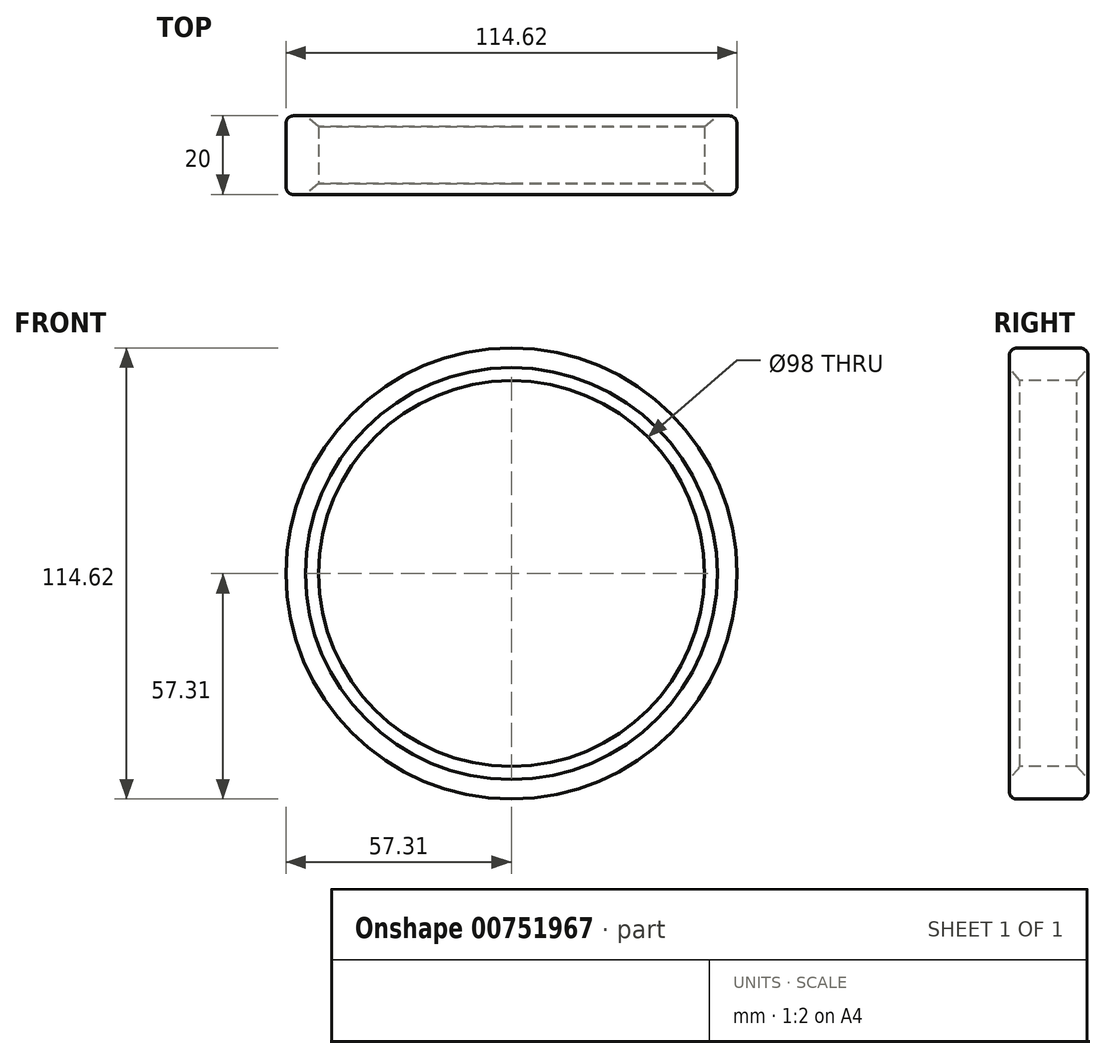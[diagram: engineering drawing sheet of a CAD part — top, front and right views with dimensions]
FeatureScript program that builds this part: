
annotation { "Feature Type Name" : "Feature", "Feature Type Description" : "" }
export const myFeature = defineFeature(function(context is Context, id is Id, definition is map)
    precondition{}
    {
        {
            var Q0;
            Q0=qCreatedBy(makeId("Top.planeOp"),FACE);
            var sketch = newSketch(context, id + "F0", { "sketchPlane" : qUnion([Q0])});
            skLineSegment(sketch, "E0", {"start": v(49, 7.25) * mm, "end": v(49, -7.25) * mm});
            skLineSegment(sketch, "E1", {"start": v(49, -7.25) * mm, "end": v(52.3, -10) * mm});
            skLineSegment(sketch, "E2", {"start": v(52.3, -10) * mm, "end": v(57.3, -10) * mm});
            skLineSegment(sketch, "E3", {"start": v(57.3, -10) * mm, "end": v(57.3, 10) * mm});
            skLineSegment(sketch, "E4", {"start": v(57.3, 10) * mm, "end": v(52.3, 10) * mm});
            skLineSegment(sketch, "E5", {"start": v(52.3, 10) * mm, "end": v(49, 7.25) * mm});
            skSolve(sketch);
        }
        {
            var Q0;
            Q0=qCreatedBy(makeId("Top.planeOp"),FACE);
            var sketch = newSketch(context, id + "F1", { "sketchPlane" : qUnion([Q0])});
            skLineSegment(sketch, "E6", {"start": v(0, -52.01) * mm, "end": v(0, 38.37) * mm});
            skSolve(sketch);
        }
        {
            var Q0;
            Q0 = qSketchRegion(id + "F0", true);
            var Q1;
            Q1=sQuery(id+"F1.wireOp",EDGE,"E6");
            revolve(context, id + "F2", {"surfaceOperationType" : NewSurfaceOperationType.NEW, "entities" : qUnion([Q0]), "axis" : qUnion([Q1]), "revolveType" : RevolveType.FULL});
        }
        {
            var Q0;
            Q0=makeQuery(id+"F2.opRevolve","SWEPT_EDGE",EDGE,{"disambiguationData":[OSD([sQuery(id+"F0.wireOp",EDGE,"E2"),sQuery(id+"F0.wireOp",EDGE,"E3")])]});
            fillet(context, id + "F3", {"entities" : qUnion([Q0]), "radius" : 2 * mm, "tangentPropagation" : true, "allowEdgeOverflow" : false});
        }
        {
            var Q0;
            Q0=makeQuery(id+"F2.opRevolve","SWEPT_EDGE",EDGE,{"disambiguationData":[OSD([sQuery(id+"F0.wireOp",EDGE,"E3"),sQuery(id+"F0.wireOp",EDGE,"E4")])]});
            fillet(context, id + "F4", {"entities" : qUnion([Q0]), "radius" : 2 * mm, "tangentPropagation" : true, "allowEdgeOverflow" : false});
        }
    });
